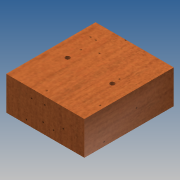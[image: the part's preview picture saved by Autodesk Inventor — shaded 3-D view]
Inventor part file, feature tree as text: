
AUTODESK INVENTOR PART (.ipt)
format: ipt  version: 2014 SP1 (Build 180222100, 222)  size: 121,344 bytes
history: native  units: in
note: dims shown in document units (in); Inventor stores cm internally (conversion verified against a paired STEP export)
features: sketch x3, hole x2, extrude x1
ambient origin geometry x8: Origin, YZ Plane, XZ Plane, XY Plane, X Axis, Y Axis, Z Axis, Center Point
bodies: Solid1 (feature_tree)
feature tree (6):
  extrude  "Extrusion1"  Depth=1.5in
  hole  "Hole1"  [1 undecoded]
  hole  "Hole2"  [1 undecoded]
  sketch  "Sketch1"  dims[d0=3.5in d1=1.5in]
  sketch  "Sketch3"  dims[d2=4.0in d3=0.0in d4=0.75in]
  sketch  "Sketch4"  dims[d5=0.201in d6=0.75in d7=0.385in d8=0.25in d9=0.5635in d10=1.0in d11=0.8108in d12=0.75in d13=0.5in d14=0.201in d15=0.75in d16=0.385in d17=0.25in d18=0.5635in d19=1.0in d20=0.8108in]
note: 2 required parameter values undecoded (feature->parameter linkage not recoverable at this tier; creation-order binding heuristic only, values carry confidence <= 0.55)
